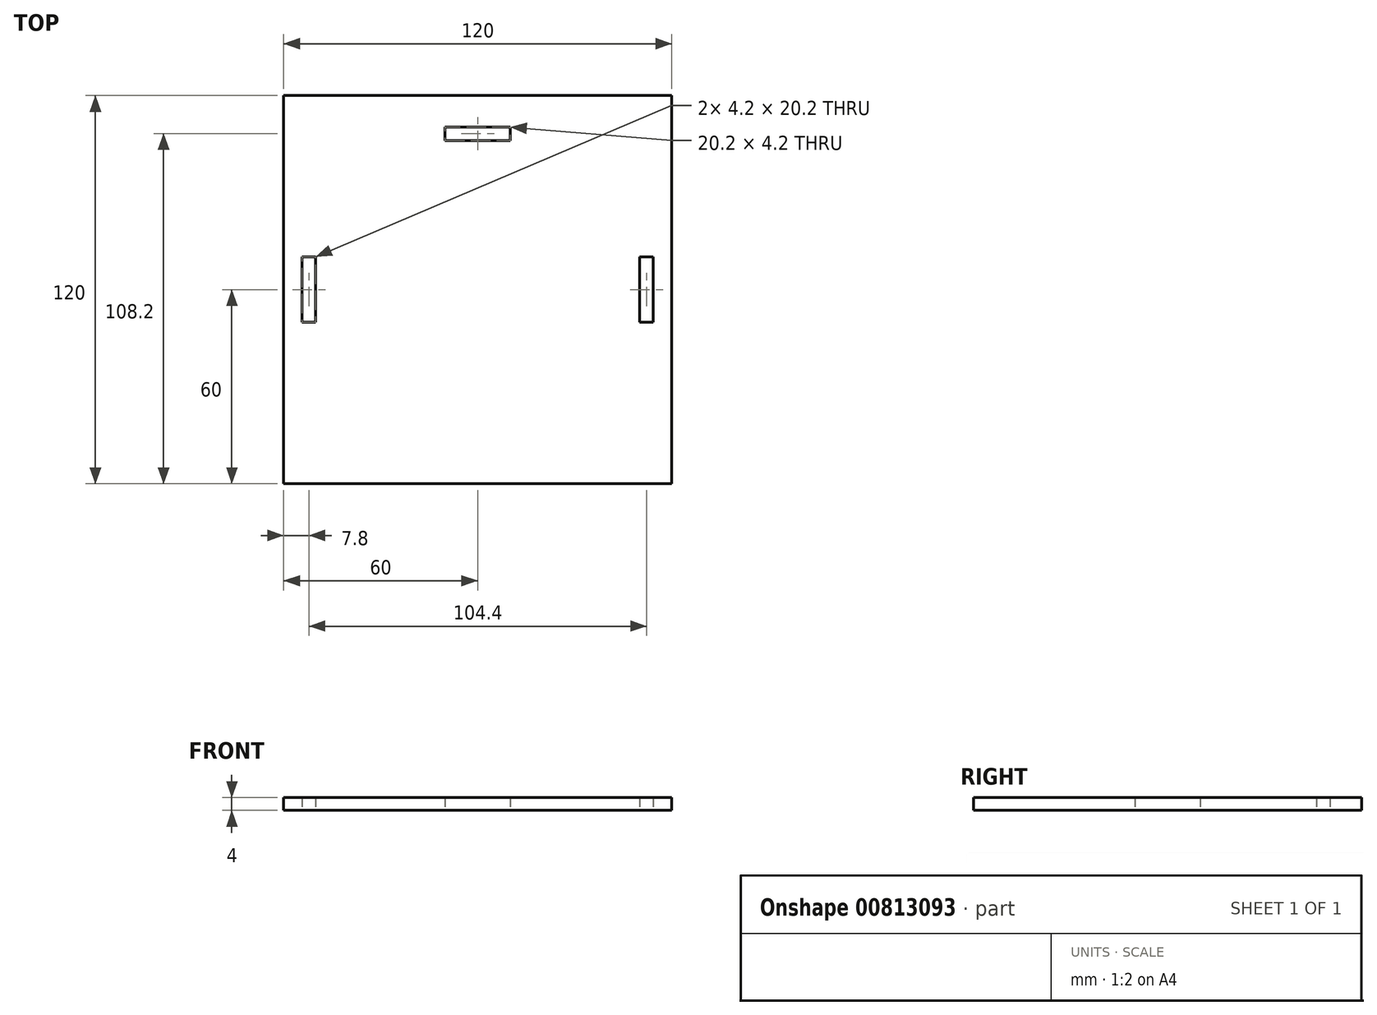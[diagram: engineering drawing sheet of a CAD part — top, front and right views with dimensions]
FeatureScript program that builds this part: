
annotation { "Feature Type Name" : "Feature", "Feature Type Description" : "" }
export const myFeature = defineFeature(function(context is Context, id is Id, definition is map)
    precondition{}
    {
        {
            var Q0;
            Q0=qCreatedBy(makeId("Top.planeOp"),FACE);
            var sketch = newSketch(context, id + "F0", { "sketchPlane" : qUnion([Q0])});
            skLineSegment(sketch, "E0.bottom", {"start": v(-60, 60) * mm, "end": v(60, 60) * mm});
            skLineSegment(sketch, "E0.top", {"start": v(-60, -60) * mm, "end": v(60, -60) * mm});
            skLineSegment(sketch, "E0.left", {"start": v(-60, 60) * mm, "end": v(-60, -60) * mm});
            skLineSegment(sketch, "E0.right", {"start": v(60, 60) * mm, "end": v(60, -60) * mm});
            skPoint(sketch, "E0.middle", {"position": v(0, 0) * mm});
            skLineSegment(sketch, "E1.bottom", {"start": v(-10.1, 50.3) * mm, "end": v(10.1, 50.3) * mm});
            skLineSegment(sketch, "E1.top", {"start": v(-10.1, 46.1) * mm, "end": v(10.1, 46.1) * mm});
            skLineSegment(sketch, "E1.left", {"start": v(-10.1, 50.3) * mm, "end": v(-10.1, 46.1) * mm});
            skLineSegment(sketch, "E1.right", {"start": v(10.1, 50.3) * mm, "end": v(10.1, 46.1) * mm});
            skPoint(sketch, "E1.middle", {"position": v(0, 48.2) * mm});
            skLineSegment(sketch, "E2.bottom", {"start": v(-54.3, 10.1) * mm, "end": v(-50.1, 10.1) * mm});
            skLineSegment(sketch, "E2.top", {"start": v(-54.3, -10.1) * mm, "end": v(-50.1, -10.1) * mm});
            skLineSegment(sketch, "E2.left", {"start": v(-54.3, 10.1) * mm, "end": v(-54.3, -10.1) * mm});
            skLineSegment(sketch, "E2.right", {"start": v(-50.1, 10.1) * mm, "end": v(-50.1, -10.1) * mm});
            skPoint(sketch, "E2.middle", {"position": v(-52.2, 0) * mm});
            skLineSegment(sketch, "E3.MirrorCS", {"start": v(54.3, -10.1) * mm, "end": v(50.1, -10.1) * mm});
            skLineSegment(sketch, "E4.MirrorCS", {"start": v(54.3, 10.1) * mm, "end": v(54.3, -10.1) * mm});
            skLineSegment(sketch, "E5.MirrorCS", {"start": v(50.1, 10.1) * mm, "end": v(50.1, -10.1) * mm});
            skPoint(sketch, "E6.MirrorP", {"position": v(52.2, 0) * mm});
            skLineSegment(sketch, "E7.MirrorCS", {"start": v(54.3, 10.1) * mm, "end": v(50.1, 10.1) * mm});
            skSolve(sketch);
        }
        {
            var Q0;
            Q0=makeQuery(id+"F0.imprint","IMPRINT",FACE,{"disambiguationData":[TD([[makeQuery(id+"F0.imprint","IMPRINT",EDGE,{"derivedFrom":sQuery(id+"F0.wireOp",EDGE,"E0.bottom")}),-1.0]])]});
            extrude(context, id + "F1", {"entities" : qUnion([Q0]), "depth" : 4 * mm, "offsetDistance" : 25 * mm});
        }
    });
